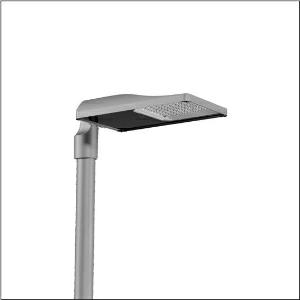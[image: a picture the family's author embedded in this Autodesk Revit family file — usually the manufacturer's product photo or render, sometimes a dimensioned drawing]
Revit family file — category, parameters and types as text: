
# Revit family: streetlight_sl_31_midi___pl52_5xh7h4aa08ma_ed53
name_source: partatom
category: Lighting Fixtures
units: mm (PartAtom-declared; Revit-internal decimal feet)

## family parameters
Cut with Voids When Loaded = No
Host = Face
Light Source = No
Part Type = Normal
Room Calculation Point = No
Round Connector Dimension = Use Diameter
Shared = No

## types (1)
- --- (1 x LED, 19840 lm, 145.3 W, 4000K)
    Apparent Load = 145 VA
    CIE Flux Codes = 27 59 98 100 100
    Color Rendering = 70
    Color Temperature = 4000K
    Default Elevation = 1800 mm
    Description = Streetlight SL 31 midi, mast luminaire, primary light control with lens, of PMMA, primary optical cover: cover, of toughened safety glass, transparent, light distribution: PL52, light emission: direct distribution, primary light characteristic: asymmetric, installation type: post-top, side-entry, LED, High Power LED, rated luminous flux: 19.840lm, luminous efficacy: 137lm/W, light colour: 740, colour temperature: 4000K, control: presetting dimming linear, flexible luminous flux parameterisation, time-dependent luminous flux control, constant luminous flux control, power reduction, intelligent temperature release in ECG and LED module, overheat protection, with cable H07RN-F 3x 1.5mm², mains connection: 220..240V, AC, 50/60Hz, connection cable pre-assembled, cable length: 10,5m, start of lifetime: 145W, end of service life: 162W, reduction: 61W, luminaire housing, of diecast aluminium, powder-coated, Siteco® metallic grey (DB 702S), corrosivity category C5 high according to DIN EN ISO 12944, no sealing on luminaire upper side, inclination: -15°..+20° (post-top) | -20°..+20° (side-entry), adjustable in 5° steps, mast flange (76/60mm) included as standard, multi-level sealing system, sealing non-destructively replaceable, protection rating (complete): IP66, insulation class (complete): insulation class II (safety insulation), certification: CE, ENEC, ENEC+, VDE, UKCA, impact resistance: IK09, permissible operating ambient temperature for outdoor applications: -40..+50°C, standard-compliant lighting for roads and squares, packaging unit: 1 piece

Light Distribution: PL52
    Height = 79 mm
    Lamp = 1 x LED
    Lamp Light Flux = 19840 lm
    Lamp Power = 145.3 W
    Lamp count = 1
    Length = 577 mm
    Luminous efficacy = 137 lm/W
    Manufacturer = Siteco
    ModVariant = No
    Model = 5XH7H4AA08MA
    Number of Poles = 1
    OnlyDefault = Yes
    Power Factor = 1
    Product Name = Streetlight SL 31 midi | PL52
    Product group = mast luminaire | pylon top
    ProductGroupID = 6100
    Protection Class = Protection class II
    Protection Degree = IP 66
    RLX_Detail_Level = 1
    RLX_Emergency_Light_Flux = 0 lm
    RLX_Emergency_Type = 0
    RLX_Emergency_Type_DB = No
    RlxData = <blob elided: 52617 chars, md5=65f587af>
    Socket = socket
    Standby Power = 0 W
    System Light Flux = 19841 lm
    System Power = 145 W
    Type Comments = factory setting: luminous flux: 100 % | dim-lin: 254 | 747 mA
    Type Image = l_1300317.jpg
    URL = http://relux.com
    VarID = @adj_016163
    Voltage = 0 V
    Weight = 0.00 kg
    Width = 362 mm

## geometry (parser evidence)
native form markers: Blend x4, Sweep x11
no freeform markers — native parametric forms only
